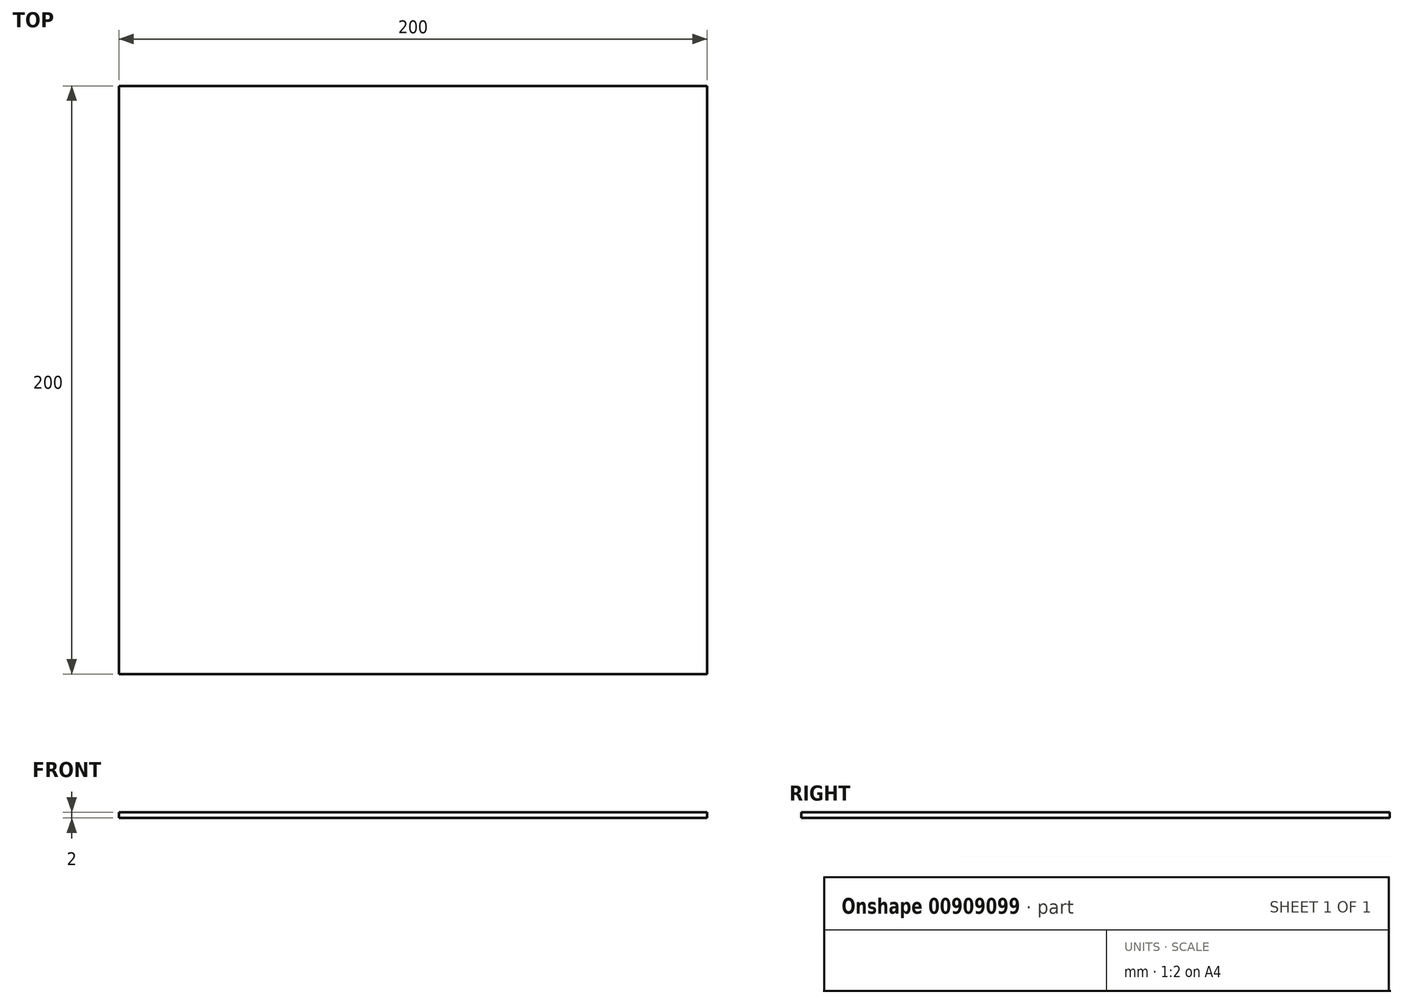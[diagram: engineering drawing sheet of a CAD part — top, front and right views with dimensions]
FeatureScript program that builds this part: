
annotation { "Feature Type Name" : "Feature", "Feature Type Description" : "" }
export const myFeature = defineFeature(function(context is Context, id is Id, definition is map)
    precondition{}
    {
        {
            var Q0;
            Q0=qCreatedBy(makeId("Top.planeOp"),FACE);
            var sketch = newSketch(context, id + "F0", { "sketchPlane" : qUnion([Q0])});
            skLineSegment(sketch, "E0.bottom", {"start": v(-100, 100) * mm, "end": v(100, 100) * mm});
            skLineSegment(sketch, "E0.top", {"start": v(-100, -100) * mm, "end": v(100, -100) * mm});
            skLineSegment(sketch, "E0.left", {"start": v(-100, 100) * mm, "end": v(-100, -100) * mm});
            skLineSegment(sketch, "E0.right", {"start": v(100, 100) * mm, "end": v(100, -100) * mm});
            skPoint(sketch, "E0.middle", {"position": v(0, 0) * mm});
            skSolve(sketch);
        }
        {
            var Q0;
            Q0=makeQuery(id+"F0.imprint","IMPRINT",FACE,{"disambiguationData":[TD([[makeQuery(id+"F0.imprint","IMPRINT",EDGE,{"derivedFrom":sQuery(id+"F0.wireOp",EDGE,"E0.bottom")}),-1.0]])]});
            extrude(context, id + "F1", {"entities" : qUnion([Q0]), "depth" : 2 * mm, "offsetDistance" : 25.4 * mm});
        }
    });
